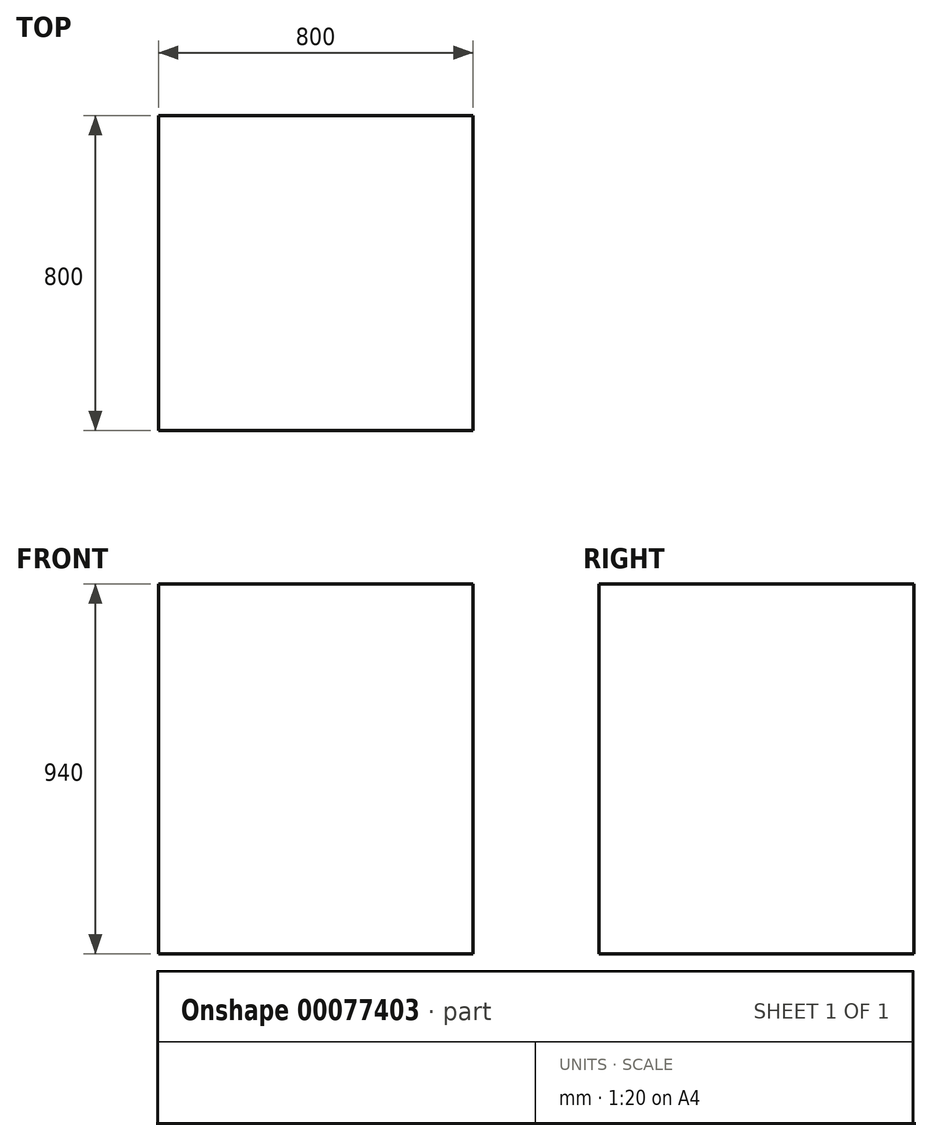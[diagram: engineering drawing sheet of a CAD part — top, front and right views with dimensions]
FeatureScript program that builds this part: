
annotation { "Feature Type Name" : "Feature", "Feature Type Description" : "" }
export const myFeature = defineFeature(function(context is Context, id is Id, definition is map)
    precondition{}
    {
        {
            var Q0;
            Q0=qCreatedBy(makeId("Front.planeOp"),FACE);
            var sketch = newSketch(context, id + "F0", { "sketchPlane" : qUnion([Q0])});
            skLineSegment(sketch, "E0.bottom", {"start": v(400, -470) * mm, "end": v(-400, -470) * mm});
            skLineSegment(sketch, "E0.top", {"start": v(400, 470) * mm, "end": v(-400, 470) * mm});
            skLineSegment(sketch, "E0.left", {"start": v(400, -470) * mm, "end": v(400, 470) * mm});
            skLineSegment(sketch, "E0.right", {"start": v(-400, -470) * mm, "end": v(-400, 470) * mm});
            skPoint(sketch, "E0.middle", {"position": v(0, 0) * mm});
            skSolve(sketch);
        }
        {
            var Q0;
            Q0=makeQuery(id+"F0.imprint","IMPRINT",FACE,{"disambiguationData":[TD([[makeQuery(id+"F0.imprint","IMPRINT",EDGE,{"derivedFrom":sQuery(id+"F0.wireOp",EDGE,"E0.bottom")}),-1.0]])]});
            extrude(context, id + "F1", {"entities" : qUnion([Q0]), "oppositeDirection" : true, "depth" : 800 * mm});
        }
    });
